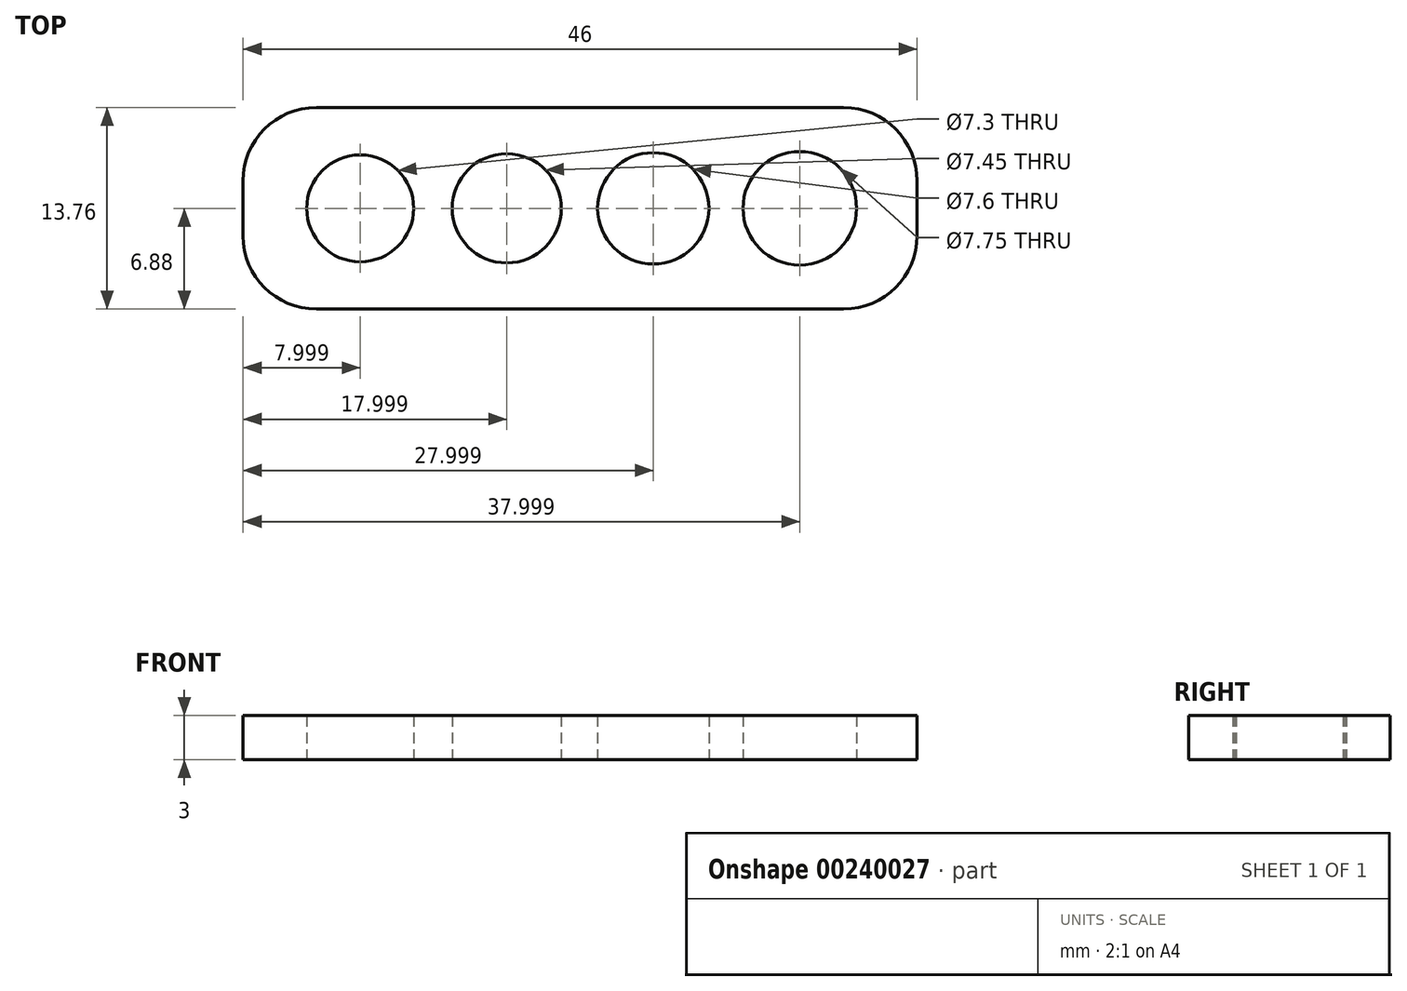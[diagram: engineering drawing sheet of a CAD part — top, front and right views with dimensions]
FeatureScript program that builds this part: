
annotation { "Feature Type Name" : "Feature", "Feature Type Description" : "" }
export const myFeature = defineFeature(function(context is Context, id is Id, definition is map)
    precondition{}
    {
        {
            var Q0;
            Q0=qCreatedBy(makeId("Top.planeOp"),FACE);
            var sketch = newSketch(context, id + "F0", { "sketchPlane" : qUnion([Q0])});
            skLineSegment(sketch, "E0.bottom", {"start": v(-22.28, 6.88) * mm, "end": v(23.72, 6.88) * mm});
            skLineSegment(sketch, "E0.top", {"start": v(-22.28, -6.88) * mm, "end": v(23.72, -6.88) * mm});
            skLineSegment(sketch, "E0.left", {"start": v(-22.28, 6.88) * mm, "end": v(-22.28, -6.87) * mm});
            skLineSegment(sketch, "E0.right", {"start": v(23.72, 6.88) * mm, "end": v(23.72, -6.87) * mm});
            skCircle(sketch, "E1", {"center": v(-14.28, 0) * mm, "radius": 3.65 * mm});
            skCircle(sketch, "E2", {"center": v(-4.28, 0) * mm, "radius": 3.73 * mm});
            skCircle(sketch, "E3", {"center": v(5.72, 0) * mm, "radius": 3.8 * mm});
            skCircle(sketch, "E4", {"center": v(15.72, 0) * mm, "radius": 3.88 * mm});
            skSolve(sketch);
        }
        {
            var Q0;
            Q0=makeQuery(id+"F0.imprint","IMPRINT",FACE,{"disambiguationData":[TD([[makeQuery(id+"F0.imprint","IMPRINT",EDGE,{"derivedFrom":sQuery(id+"F0.wireOp",EDGE,"E0.bottom")}),-1.0]])]});
            extrude(context, id + "F1", {"entities" : qUnion([Q0]), "depth" : 3 * mm});
        }
        {
            var Q0;
            Q0=makeQuery(id+"F1.opExtrude","SWEPT_EDGE",EDGE,{"disambiguationData":[OSD([sQuery(id+"F0.wireOp",EDGE,"E0.bottom"),sQuery(id+"F0.wireOp",EDGE,"E0.left")])]});
            var Q1;
            Q1=makeQuery(id+"F1.opExtrude","SWEPT_EDGE",EDGE,{"disambiguationData":[OSD([sQuery(id+"F0.wireOp",EDGE,"E0.top"),sQuery(id+"F0.wireOp",EDGE,"E0.left")])]});
            var Q2;
            Q2=makeQuery(id+"F1.opExtrude","SWEPT_EDGE",EDGE,{"disambiguationData":[OSD([sQuery(id+"F0.wireOp",EDGE,"E0.top"),sQuery(id+"F0.wireOp",EDGE,"E0.right")])]});
            var Q3;
            Q3=makeQuery(id+"F1.opExtrude","SWEPT_EDGE",EDGE,{"disambiguationData":[OSD([sQuery(id+"F0.wireOp",EDGE,"E0.bottom"),sQuery(id+"F0.wireOp",EDGE,"E0.right")])]});
            fillet(context, id + "F2", {"entities" : qUnion([Q0, Q1, Q2, Q3]), "radius" : 5 * mm, "tangentPropagation" : true, "allowEdgeOverflow" : false});
        }
    });
